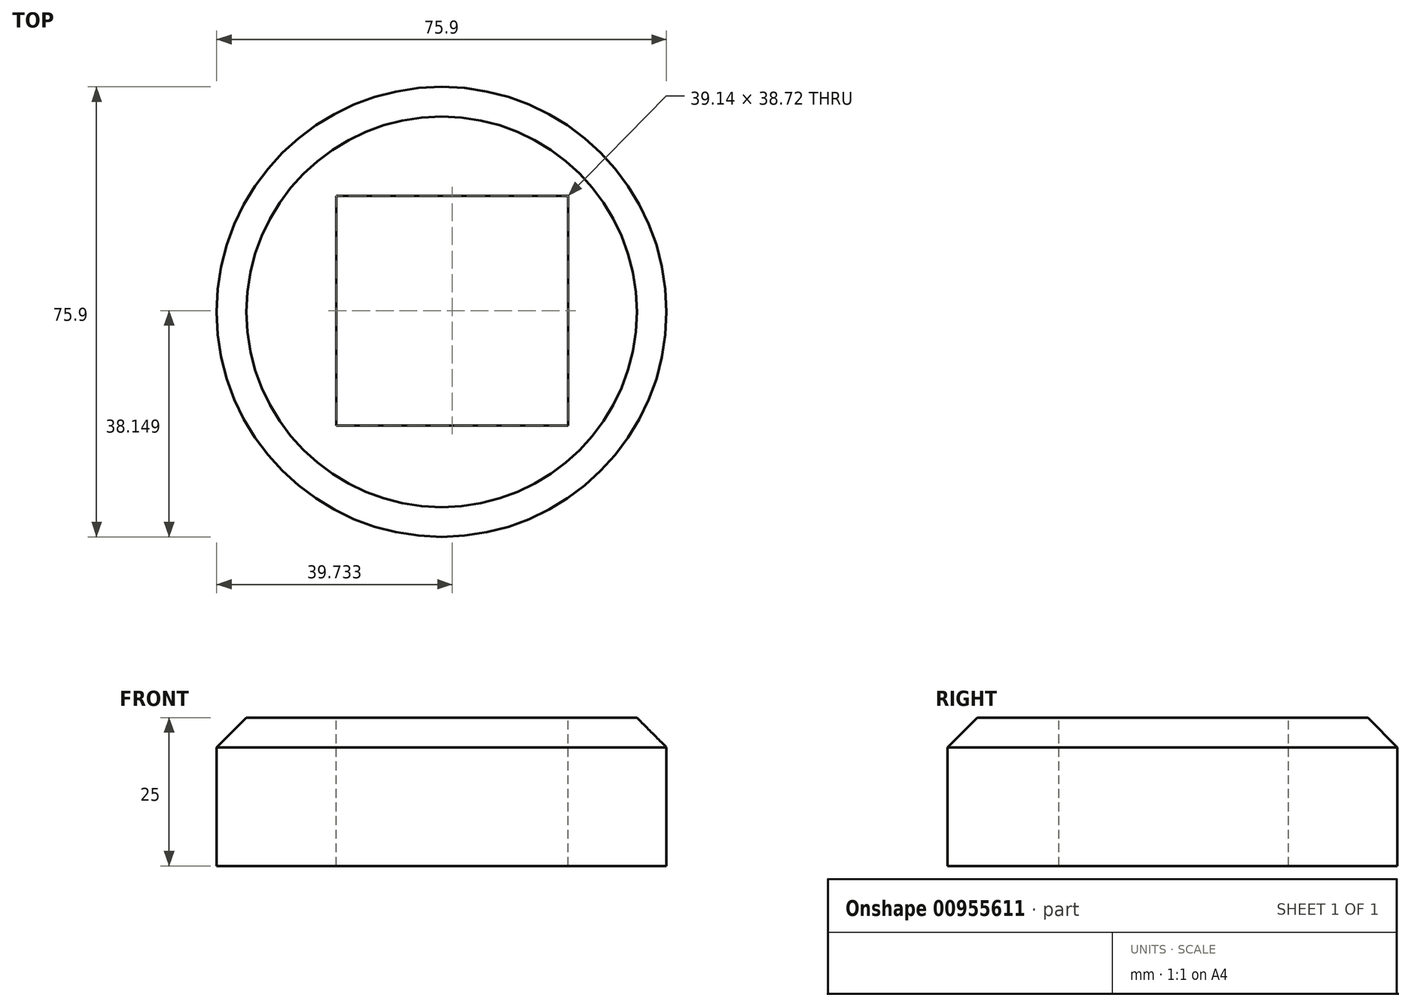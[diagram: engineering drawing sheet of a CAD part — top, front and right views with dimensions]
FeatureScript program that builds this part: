
annotation { "Feature Type Name" : "Feature", "Feature Type Description" : "" }
export const myFeature = defineFeature(function(context is Context, id is Id, definition is map)
    precondition{}
    {
        {
            var Q0;
            Q0=qCreatedBy(makeId("Top.planeOp"),FACE);
            var sketch = newSketch(context, id + "F0", { "sketchPlane" : qUnion([Q0])});
            skCircle(sketch, "E0", {"center": v(0, 0) * mm, "radius": 37.95 * mm});
            skSolve(sketch);
        }
        {
            var Q0;
            Q0=makeQuery(id+"F0.imprint","IMPRINT",FACE,{"disambiguationData":[TD([[makeQuery(id+"F0.imprint","IMPRINT",EDGE,{"derivedFrom":sQuery(id+"F0.wireOp",EDGE,"E0")}),1.0]])]});
            extrude(context, id + "F1", {"entities" : qUnion([Q0]), "depth" : 25 * mm, "offsetDistance" : 25 * mm});
        }
        {
            var Q0;
            Q0=makeQuery(id+"F1.opExtrude","CAP_FACE",FACE,{"disambiguationData":[OSD([sQuery(id+"F0.wireOp",EDGE,"E0")])],"isStart":false});
            var sketch = newSketch(context, id + "F2", { "sketchPlane" : qUnion([Q0])});
            skLineSegment(sketch, "E1.bottom", {"start": v(-17.79, 19.56) * mm, "end": v(21.35, 19.56) * mm});
            skLineSegment(sketch, "E1.top", {"start": v(-17.79, -19.16) * mm, "end": v(21.35, -19.16) * mm});
            skLineSegment(sketch, "E1.left", {"start": v(-17.79, 19.56) * mm, "end": v(-17.79, -19.16) * mm});
            skLineSegment(sketch, "E1.right", {"start": v(21.35, 19.56) * mm, "end": v(21.35, -19.16) * mm});
            skSolve(sketch);
        }
        {
            var Q0;
            Q0=makeQuery(id+"F2.imprint","IMPRINT",FACE,{"disambiguationData":[TD([[makeQuery(id+"F2.imprint","IMPRINT",EDGE,{"derivedFrom":sQuery(id+"F2.wireOp",EDGE,"E1.bottom")}),-1.0]])]});
            extrude(context, id + "F3", {"entities" : qUnion([Q0]), "operationType" : NewBodyOperationType.REMOVE, "oppositeDirection" : true, "depth" : 25 * mm, "offsetDistance" : 25 * mm});
        }
        {
            var Q0;
            Q0=makeQuery(id+"F1.opExtrude","CAP_EDGE",EDGE,{"disambiguationData":[OSD([sQuery(id+"F0.wireOp",EDGE,"E0")])],"isStart":false});
            chamfer(context, id + "F4", {"entities" : qUnion([Q0]), "width" : 5 * mm, "tangentPropagation" : true});
        }
    });
